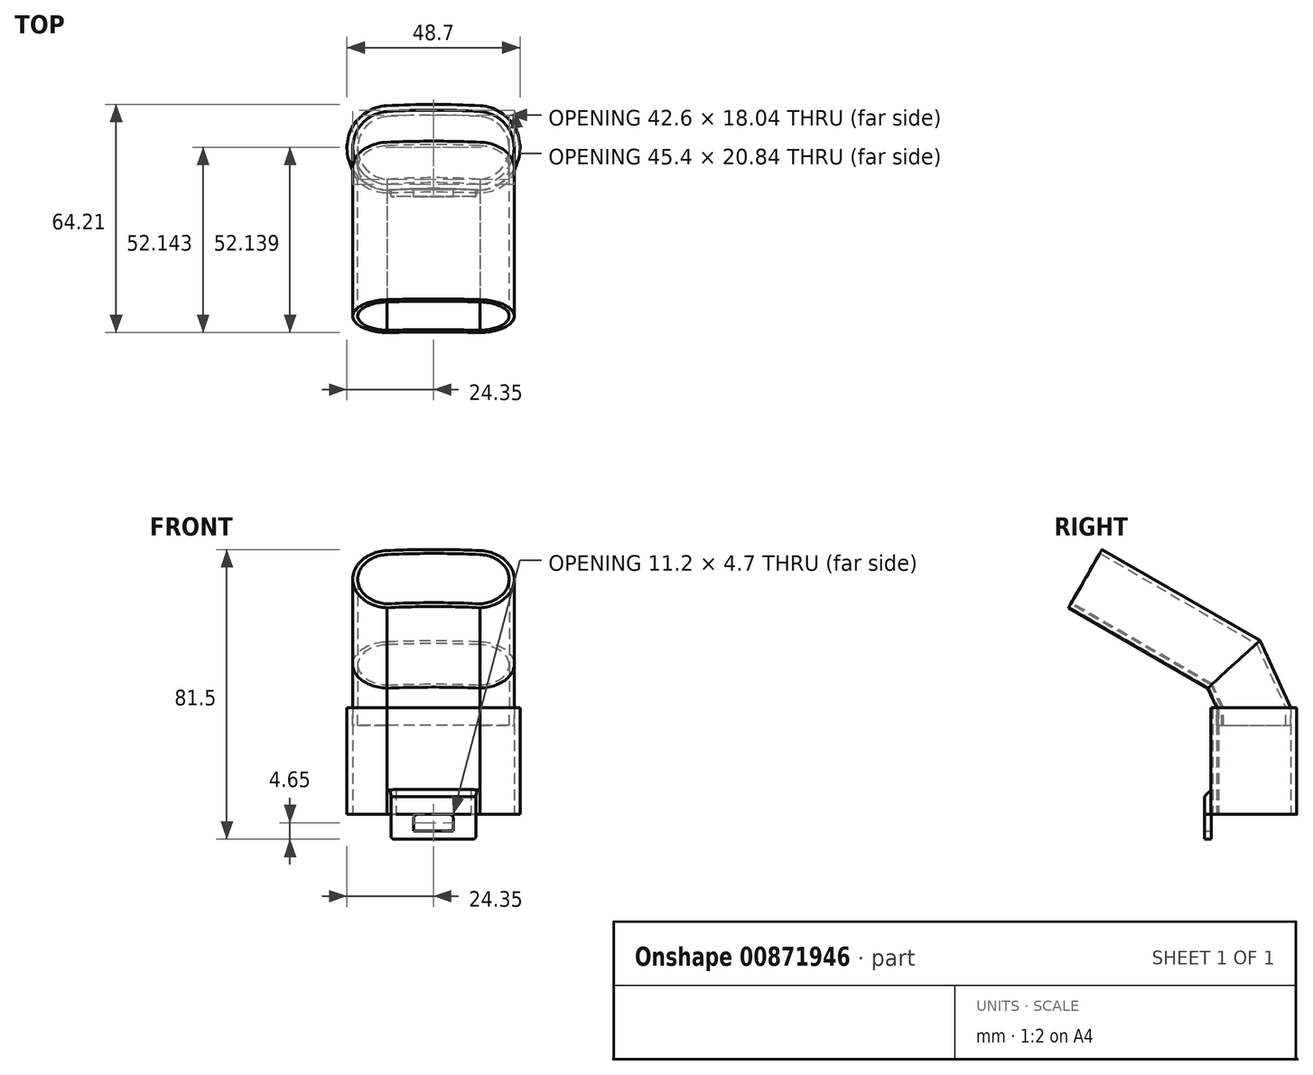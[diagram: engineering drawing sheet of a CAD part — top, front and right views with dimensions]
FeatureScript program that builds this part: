
annotation { "Feature Type Name" : "Feature", "Feature Type Description" : "" }
export const myFeature = defineFeature(function(context is Context, id is Id, definition is map)
    precondition{}
    {
        {
            var Q0;
            Q0=qCreatedBy(makeId("Top.planeOp"),FACE);
            var sketch = newSketch(context, id + "F0", { "sketchPlane" : qUnion([Q0])});
            skArc(sketch, "E0", {"start": v(13.08, 0) * mm, "mid": v(0, 0.44) * mm, "end": v(-13.08, 0) * mm});
            skArc(sketch, "E1", {"start": v(13.08, 20.44) * mm, "mid": v(0, 20.84) * mm, "end": v(-13.08, 20.44) * mm});
            skArc(sketch, "E2", {"start": v(-13.08, 20.44) * mm, "mid": v(-22.7, 10.22) * mm, "end": v(-13.08, 0) * mm});
            skArc(sketch, "E3", {"start": v(13.08, 0) * mm, "mid": v(22.7, 10.22) * mm, "end": v(13.08, 20.44) * mm});
            skArc(sketch, "E4.0", {"start": v(13.18, 22.09) * mm, "mid": v(0, 22.49) * mm, "end": v(-13.18, 22.09) * mm});
            skArc(sketch, "E4.1", {"start": v(13.07, -1.65) * mm, "mid": v(24.35, 10.17) * mm, "end": v(13.18, 22.09) * mm});
            skArc(sketch, "E4.2", {"start": v(13.07, -1.65) * mm, "mid": v(0, -1.21) * mm, "end": v(-13.07, -1.65) * mm});
            skArc(sketch, "E4.3", {"start": v(-13.18, 22.09) * mm, "mid": v(-24.35, 10.17) * mm, "end": v(-13.07, -1.65) * mm});
            skSolve(sketch);
        }
        {
            var Q0;
            Q0 = qSketchRegion(id + "F0", true);
            extrude(context, id + "F1", {"entities" : qUnion([Q0]), "depth" : 30 * mm, "offsetDistance" : 25 * mm});
        }
        {
            var Q0;
            Q0=qCreatedBy(makeId("Front.planeOp"),FACE);
            cPlane(context, id + "F2", {"entities" : qUnion([Q0]), "cplaneType" : CPlaneType.OFFSET, "offset" : 1.5 * mm, "width" : 150 * mm, "height" : 150 * mm});
        }
        {
            var Q0;
            Q0=qCreatedBy(id+"F2.planeOp",FACE);
            var sketch = newSketch(context, id + "F3", { "sketchPlane" : qUnion([Q0])});
            skLineSegment(sketch, "E5.bottom", {"start": v(12, -7) * mm, "end": v(-12, -7) * mm});
            skLineSegment(sketch, "E5.top", {"start": v(12, 7) * mm, "end": v(-12, 7) * mm});
            skLineSegment(sketch, "E5.left", {"start": v(12, -7) * mm, "end": v(12, 7) * mm});
            skLineSegment(sketch, "E5.right", {"start": v(-12, -7) * mm, "end": v(-12, 7) * mm});
            skPoint(sketch, "E5.middle", {"position": v(0, 0) * mm});
            skSolve(sketch);
        }
        {
            var Q0;
            Q0 = qSketchRegion(id + "F3", true);
            extrude(context, id + "F4", {"entities" : qUnion([Q0]), "operationType" : NewBodyOperationType.ADD, "depth" : 2 * mm, "offsetDistance" : 25 * mm});
        }
        {
            var Q0;
            Q0=makeQuery(id+"F4.boolean.opBoolean","INTERSECT",EDGE,{"derivedFrom":[makeQuery(id+"F1.opExtrude","SWEPT_FACE",FACE,{"disambiguationData":[OSD([sQuery(id+"F0.wireOp",EDGE,"E4.2")])]}),makeQuery(id+"F4.opExtrude","SWEPT_FACE",FACE,{"disambiguationData":[OSD([sQuery(id+"F3.wireOp",EDGE,"E5.right")])]})]});
            var Q1;
            Q1=makeQuery(id+"F4.boolean.opBoolean","INTERSECT",EDGE,{"derivedFrom":[makeQuery(id+"F1.opExtrude","SWEPT_FACE",FACE,{"disambiguationData":[OSD([sQuery(id+"F0.wireOp",EDGE,"E4.2")])]}),makeQuery(id+"F4.opExtrude","SWEPT_FACE",FACE,{"disambiguationData":[OSD([sQuery(id+"F3.wireOp",EDGE,"E5.left")])]})]});
            fillet(context, id + "F5", {"entities" : qUnion([Q0, Q1]), "radius" : 1.25 * mm, "tangentPropagation" : true, "allowEdgeOverflow" : false});
        }
        {
            var Q0;
            Q0=makeQuery(id+"F4.opExtrude","CAP_EDGE",EDGE,{"disambiguationData":[OSD([sQuery(id+"F3.wireOp",EDGE,"E5.top")])],"isStart":false});
            chamfer(context, id + "F6", {"entities" : qUnion([Q0]), "width" : 2 * mm, "tangentPropagation" : true});
        }
        {
            var Q0;
            Q0=makeQuery(id+"F4.opExtrude","SWEPT_EDGE",EDGE,{"disambiguationData":[OSD([sQuery(id+"F3.wireOp",EDGE,"E5.bottom"),sQuery(id+"F3.wireOp",EDGE,"E5.right")])]});
            var Q1;
            Q1=makeQuery(id+"F4.opExtrude","SWEPT_EDGE",EDGE,{"disambiguationData":[OSD([sQuery(id+"F3.wireOp",EDGE,"E5.bottom"),sQuery(id+"F3.wireOp",EDGE,"E5.left")])]});
            fillet(context, id + "F7", {"entities" : qUnion([Q0, Q1]), "radius" : 1 * mm, "tangentPropagation" : true, "allowEdgeOverflow" : false});
        }
        {
            var Q0;
            Q0=makeQuery(id+"F4.opExtrude","CAP_FACE",FACE,{"disambiguationData":[OSD([sQuery(id+"F3.wireOp",EDGE,"E5.bottom"),sQuery(id+"F3.wireOp",EDGE,"E5.top"),sQuery(id+"F3.wireOp",EDGE,"E5.left"),sQuery(id+"F3.wireOp",EDGE,"E5.right")])],"isStart":true});
            var sketch = newSketch(context, id + "F8", { "sketchPlane" : qUnion([Q0])});
            skLineSegment(sketch, "E6.bottom", {"start": v(-5.6, 0) * mm, "end": v(5.6, 0) * mm});
            skLineSegment(sketch, "E6.top", {"start": v(-5.6, -4.7) * mm, "end": v(5.6, -4.7) * mm});
            skLineSegment(sketch, "E6.left", {"start": v(-5.6, 0) * mm, "end": v(-5.6, -4.7) * mm});
            skLineSegment(sketch, "E6.right", {"start": v(5.6, 0) * mm, "end": v(5.6, -4.7) * mm});
            skLineSegment(sketch, "E7", {"start": v(0, 0) * mm, "end": v(0, -1.26) * mm, "construction": true});
            skSolve(sketch);
        }
        {
            var Q0;
            Q0 = qSketchRegion(id + "F8", true);
            extrude(context, id + "F9", {"entities" : qUnion([Q0]), "operationType" : NewBodyOperationType.REMOVE, "oppositeDirection" : true, "depth" : 25 * mm, "offsetDistance" : 25 * mm});
        }
        {
            var Q0;
            Q0=makeQuery(id+"F9.boolean.opBoolean","COPY",EDGE,{"derivedFrom":makeQuery(id+"F9.opExtrude","SWEPT_EDGE",EDGE,{"disambiguationData":[OSD([sQuery(id+"F8.wireOp",EDGE,"E6.bottom"),sQuery(id+"F8.wireOp",EDGE,"E6.right")])]})});
            var Q1;
            Q1=makeQuery(id+"F9.boolean.opBoolean","COPY",EDGE,{"derivedFrom":makeQuery(id+"F9.opExtrude","SWEPT_EDGE",EDGE,{"disambiguationData":[OSD([sQuery(id+"F8.wireOp",EDGE,"E6.bottom"),sQuery(id+"F8.wireOp",EDGE,"E6.left")])]})});
            fillet(context, id + "F10", {"entities" : qUnion([Q0, Q1]), "radius" : 1.2 * mm, "tangentPropagation" : true, "allowEdgeOverflow" : false});
        }
        {
            var Q0;
            Q0=makeQuery(id+"F1.opExtrude","CAP_FACE",FACE,{"disambiguationData":[OSD([sQuery(id+"F0.wireOp",EDGE,"E0"),sQuery(id+"F0.wireOp",EDGE,"E1"),sQuery(id+"F0.wireOp",EDGE,"E2"),sQuery(id+"F0.wireOp",EDGE,"E3"),sQuery(id+"F0.wireOp",EDGE,"E4.0"),sQuery(id+"F0.wireOp",EDGE,"E4.1"),sQuery(id+"F0.wireOp",EDGE,"E4.2"),sQuery(id+"F0.wireOp",EDGE,"E4.3")])],"isStart":false});
            var sketch = newSketch(context, id + "F11", { "sketchPlane" : qUnion([Q0])});
            skArc(sketch, "E8.0", {"start": v(13, 19.04) * mm, "mid": v(0, 19.44) * mm, "end": v(-13, 19.04) * mm});
            skArc(sketch, "E8.1", {"start": v(13.08, 1.4) * mm, "mid": v(21.3, 10.26) * mm, "end": v(13, 19.04) * mm});
            skArc(sketch, "E8.2", {"start": v(13.08, 1.4) * mm, "mid": v(0, 1.84) * mm, "end": v(-13.08, 1.4) * mm});
            skArc(sketch, "E8.3", {"start": v(-13, 19.04) * mm, "mid": v(-21.3, 10.26) * mm, "end": v(-13.08, 1.4) * mm});
            skSolve(sketch);
        }
        {
            var Q0;
            Q0=qCreatedBy(makeId("Right.planeOp"),FACE);
            var sketch = newSketch(context, id + "F12", { "sketchPlane" : qUnion([Q0])});
            skLineSegment(sketch, "E9", {"start": v(20.86, 30) * mm, "end": v(12.15, 48.9) * mm});
            skLineSegment(sketch, "E10", {"start": v(12.15, 48.9) * mm, "end": v(-32.28, 74.53) * mm});
            skSolve(sketch);
        }
        {
            var Q0;
            Q0=makeQuery(id+"F11.imprint","IMPRINT",FACE,{"disambiguationData":[TD([[makeQuery(id+"F11.imprint","IMPRINT",EDGE,{"derivedFrom":sQuery(id+"F11.wireOp",EDGE,"E8.0")}),-1.0]])]});
            var Q1;
            Q1=sQuery(id+"F12.wireOp",EDGE,"E9");
            var Q2;
            Q2=sQuery(id+"F12.wireOp",EDGE,"E10");
            sweep(context, id + "F13", {"profiles" : qUnion([Q0]), "path" : qUnion([Q1, Q2])});
        }
        {
            var Q0;
            Q0=makeQuery(id+"F13.opSweep","CAP_FACE",FACE,{"disambiguationData":[OSD([sQuery(id+"F0.wireOp",EDGE,"E0"),sQuery(id+"F0.wireOp",EDGE,"E1"),sQuery(id+"F0.wireOp",EDGE,"E2"),sQuery(id+"F0.wireOp",EDGE,"E3"),sQuery(id+"F11.wireOp",EDGE,"E8.0"),sQuery(id+"F11.wireOp",EDGE,"E8.1"),sQuery(id+"F11.wireOp",EDGE,"E8.2"),sQuery(id+"F11.wireOp",EDGE,"E8.3"),sQuery(id+"F12.wireOp",VERTEX,"E9.start")])],"isStart":true});
            var sketch = newSketch(context, id + "F14", { "sketchPlane" : qUnion([Q0])});
            skSolve(sketch);
        }
        {
            var Q0;
            {var subQ0=sQuery(id+"F12.wireOp",VERTEX,"E9.start");Q0=makeQuery(id+"F14.imprint","IMPRINT",FACE,{"disambiguationData":[TD([[makeQuery(id+"F14.imprint","IMPRINT",EDGE,{"derivedFrom":makeQuery(id+"F13.opSweep","CAP_EDGE",EDGE,{"disambiguationData":[OSD([sQuery(id+"F11.wireOp",EDGE,"E8.0"),subQ0])],"isStart":true})}),1.0]])]});}
            extrude(context, id + "F15", {"entities" : qUnion([Q0]), "depth" : 5 * mm, "offsetDistance" : 25 * mm});
        }
        {
            var Q0;
            Q0=qCreatedBy(makeId("Right.planeOp"),FACE);
            var sketch = newSketch(context, id + "F16", { "sketchPlane" : qUnion([Q0])});
            skLineSegment(sketch, "E11", {"start": v(-30.69, 77.24) * mm, "end": v(-45.57, 51.43) * mm});
            skLineSegment(sketch, "E12", {"start": v(-45.57, 51.43) * mm, "end": v(-62.73, 61.33) * mm});
            skLineSegment(sketch, "E13", {"start": v(-62.73, 61.33) * mm, "end": v(-30.69, 77.24) * mm});
            skSolve(sketch);
        }
        {
            var Q0;
            Q0 = qSketchRegion(id + "F16", true);
            extrude(context, id + "F17", {"entities" : qUnion([Q0]), "operationType" : NewBodyOperationType.REMOVE, "endBound" : BoundingType.SYMMETRIC, "depth" : 69.8 * mm, "offsetDistance" : 25 * mm});
        }
    });
